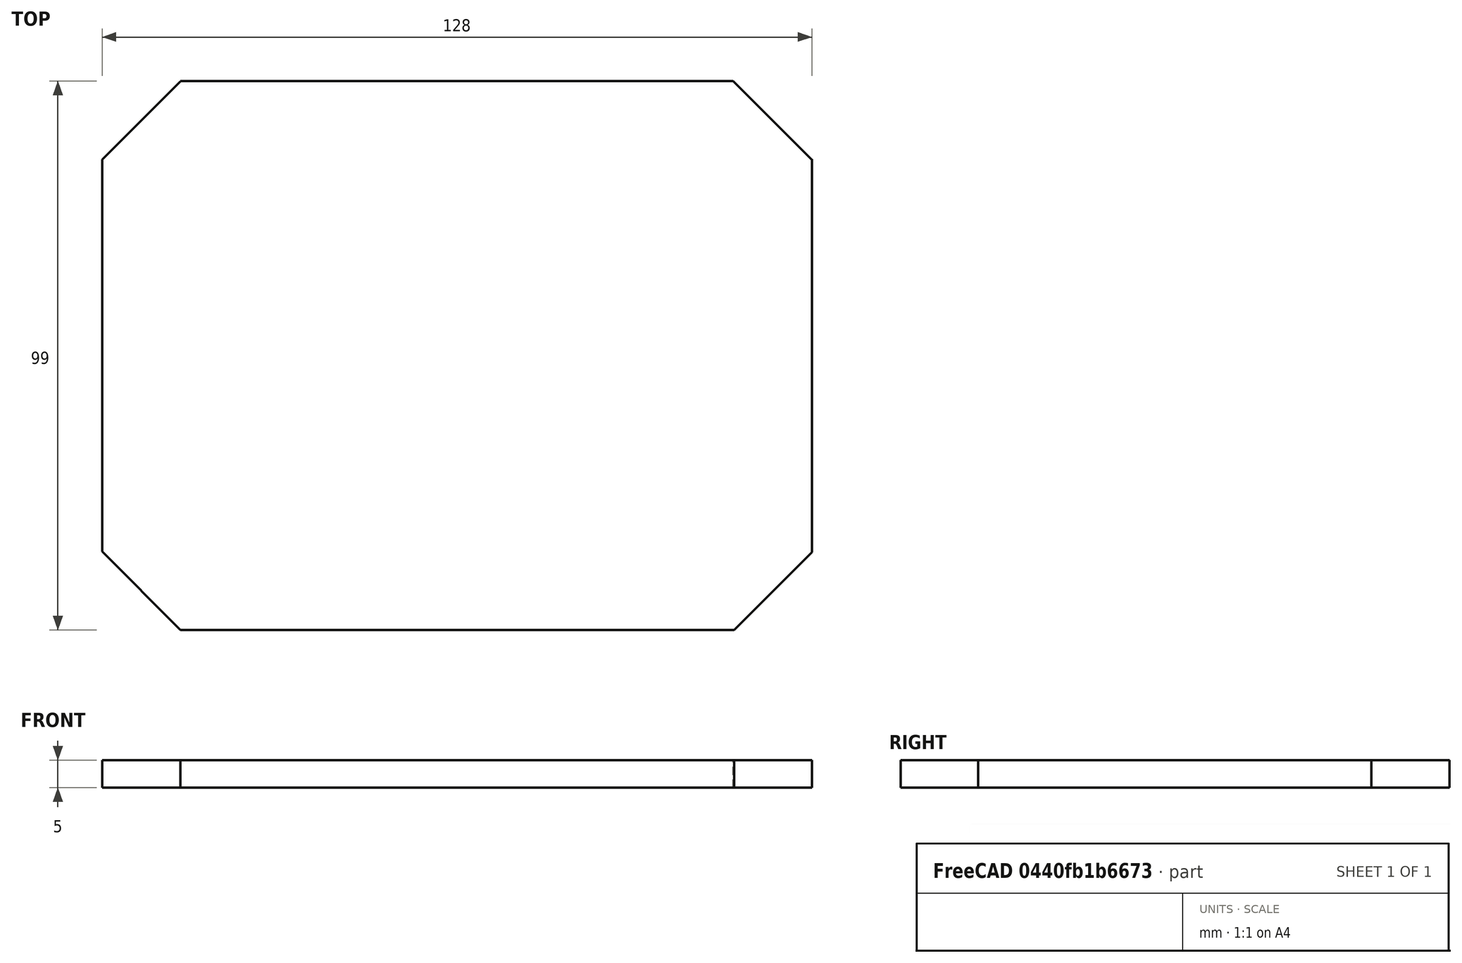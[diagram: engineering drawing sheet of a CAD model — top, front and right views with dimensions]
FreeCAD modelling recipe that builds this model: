
FCSTD DOCUMENT  (FreeCAD 0.15R4671 (Git))
Label: Base Fresada
License: All rights reserved
LicenseURL: http://en.wikipedia.org/wiki/All_rights_reserved
objects: Part::Box×5, Part::MultiFuse×1, Part::Cut×1
note: 7 computed .brp shape members not serialized (recipe doc carries the construction recipe); baked Part::Feature solids carry a one-line shape summary decoded from their .brp

FEATURE [Part::Box] Box001  label="Superficie metacrilato"
  Height = 5
  Length = 128
  Placement = pos=(-14,-14.5,0) rot=(0,0,1;0rad)
  Width = 99
FEATURE [Part::Box] Box002  label="Cubo002"
  Height = 20
  Length = 20
  Placement = pos=(100,-14.5,0) rot=(0,0,-1;0.785398rad)
  Width = 20
FEATURE [Part::Box] Box  label="Cubo003"
  Height = 20
  Length = 20
  Placement = pos=(99.8,84.5,0) rot=(0,0,-1;0.785398rad)
  Width = 20
FEATURE [Part::Box] Box003  label="Cubo004"
  Height = 20
  Length = 20
  Placement = pos=(-14,-28.65,0) rot=(0,0,1;0.785398rad)
  Width = 20
FEATURE [Part::Box] Box004  label="Cubo005"
  Height = 20
  Length = 20
  Placement = pos=(-14,70.35,0) rot=(0,0,1;0.785398rad)
  Width = 20
FEATURE [Part::MultiFuse] Fusion
  Shapes = -> [Box,Box003,Box004,Box002]
FEATURE [Part::Cut] Cut
  Base = -> Box001
  Tool = -> Fusion
